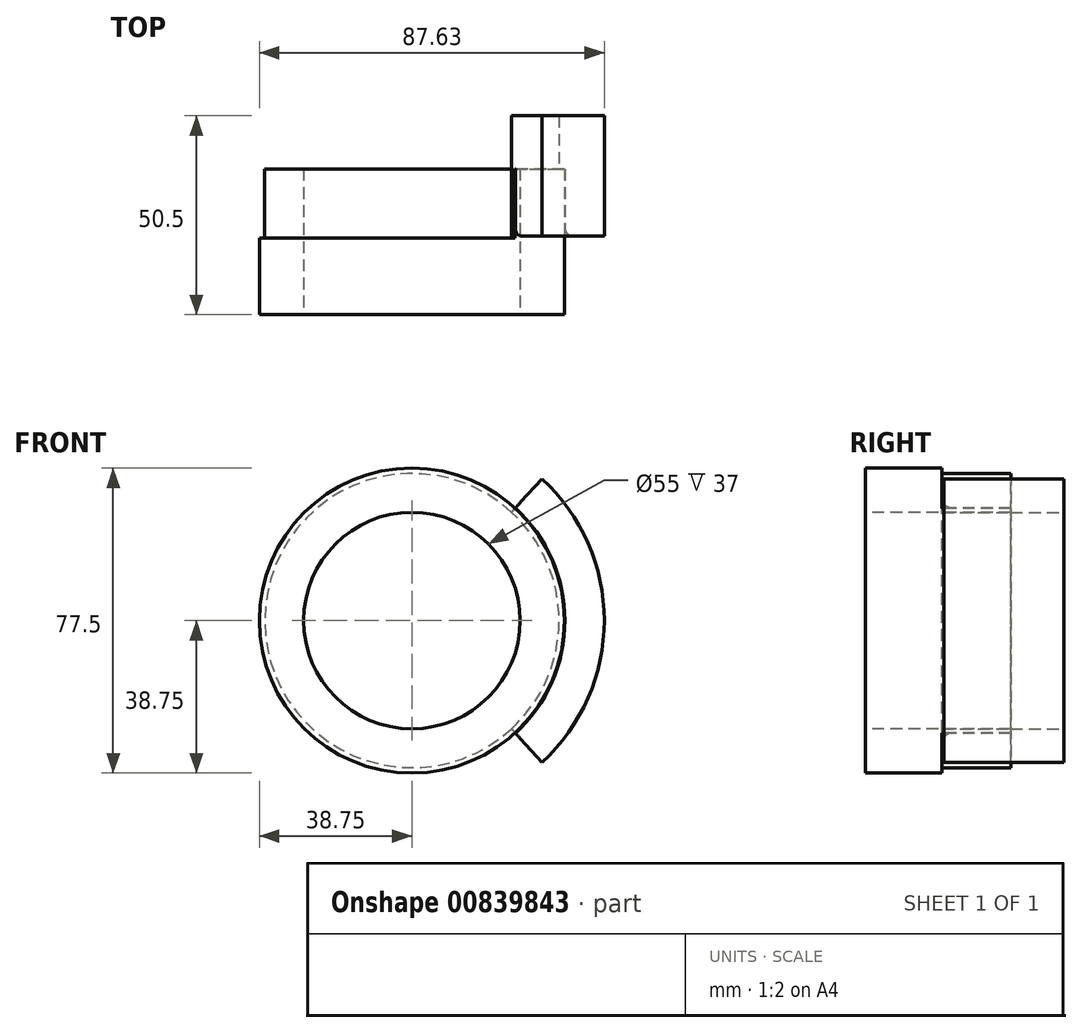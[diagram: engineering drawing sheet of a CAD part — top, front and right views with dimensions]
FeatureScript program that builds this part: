
annotation { "Feature Type Name" : "Feature", "Feature Type Description" : "" }
export const myFeature = defineFeature(function(context is Context, id is Id, definition is map)
    precondition{}
    {
        {
            var Q0;
            Q0=qCreatedBy(makeId("Front.planeOp"),FACE);
            var sketch = newSketch(context, id + "F0", { "sketchPlane" : qUnion([Q0])});
            skCircle(sketch, "E0", {"center": v(0, 0) * mm, "radius": 38.75 * mm});
            skCircle(sketch, "E1", {"center": v(0, 0) * mm, "radius": 27.5 * mm});
            skSolve(sketch);
        }
        {
            var Q0;
            Q0 = qSketchRegion(id + "F0", true);
            extrude(context, id + "F1", {"entities" : qUnion([Q0]), "oppositeDirection" : true, "depth" : 37 * mm, "offsetDistance" : 25 * mm});
        }
        {
            var Q0;
            Q0=qCreatedBy(makeId("Right.planeOp"),FACE);
            var sketch = newSketch(context, id + "F2", { "sketchPlane" : qUnion([Q0])});
            skLineSegment(sketch, "E2", {"start": v(0, 0) * mm, "end": v(0, 38.88) * mm});
            skLineSegment(sketch, "E3", {"start": v(20, 38.88) * mm, "end": v(20, 48.88) * mm});
            skLineSegment(sketch, "E4", {"start": v(20, 48.88) * mm, "end": v(50.5, 48.88) * mm});
            skLineSegment(sketch, "E5", {"start": v(50.5, 48.88) * mm, "end": v(50.5, 37.38) * mm});
            skLineSegment(sketch, "E6", {"start": v(50.5, 37.38) * mm, "end": v(37, 37.38) * mm});
            skLineSegment(sketch, "E7", {"start": v(37, 37.38) * mm, "end": v(37, 38.88) * mm});
            skLineSegment(sketch, "E8", {"start": v(37, 38.88) * mm, "end": v(20, 38.88) * mm});
            skSolve(sketch);
        }
        {
            var Q0;
            Q0=makeQuery(id+"F2.imprint","IMPRINT",FACE,{"disambiguationData":[TD([[makeQuery(id+"F2.imprint","IMPRINT",EDGE,{"derivedFrom":sQuery(id+"F2.wireOp",EDGE,"E3")}),-1.0]])]});
            var Q1;
            Q1=makeQuery(id+"F1.opExtrude","CAP_EDGE",EDGE,{"disambiguationData":[OSD([sQuery(id+"F0.wireOp",EDGE,"E0")])],"isStart":false});
            revolve(context, id + "F3", {"operationType" : NewBodyOperationType.ADD, "surfaceOperationType" : NewSurfaceOperationType.NEW, "entities" : qUnion([Q0]), "axis" : qUnion([Q1]), "revolveType" : RevolveType.FULL, "oppositeDirection" : true});
        }
        {
            var Q0;
            Q0=makeQuery(id+"F3.opRevolve","SWEPT_FACE",FACE,{"disambiguationData":[OSD([sQuery(id+"F2.wireOp",EDGE,"E5")])]});
            var sketch = newSketch(context, id + "F4", { "sketchPlane" : qUnion([Q0])});
            skLineSegment(sketch, "E9", {"start": v(-25.25, -27.5) * mm, "end": v(-33.06, -36) * mm});
            skLineSegment(sketch, "E10", {"start": v(-25.25, 27.5) * mm, "end": v(-33.06, 36) * mm});
            skPoint(sketch, "E11.center.orphan", {"position": v(0, 0) * mm});
            skArc(sketch, "E12", {"start": v(-25.28, -27.53) * mm, "mid": v(37.38, 0) * mm, "end": v(-25.28, 27.53) * mm});
            skArc(sketch, "E13", {"start": v(-33.06, -36) * mm, "mid": v(48.88, 0) * mm, "end": v(-33.06, 36) * mm});
            skSolve(sketch);
        }
        {
            var Q0;
            {var subQ0=sQuery(id+"F4.wireOp",EDGE,"E13");Q0=makeQuery(id+"F4.imprint","IMPRINT",FACE,{"disambiguationData":[TD([[makeQuery(id+"F4.imprint","IMPRINT",EDGE,{"derivedFrom":subQ0}),-1.0]])]});}
            extrude(context, id + "F5", {"entities" : qUnion([Q0]), "operationType" : NewBodyOperationType.REMOVE, "oppositeDirection" : true, "depth" : 31 * mm, "offsetDistance" : 25 * mm});
        }
        {
            var Q0;
            {var subQ0=sQuery(id+"F2.wireOp",EDGE,"E6");Q0=makeQuery(id+"F5.boolean.opBoolean","SPLIT",EDGE,{"disambiguationData":[topologyDisambiguationEdgeConnected([makeQuery(id+"F3.opRevolve","SWEPT_FACE",FACE,{"disambiguationData":[OSD([subQ0])]})])],"derivedFrom":makeQuery(id+"F3.opRevolve","SWEPT_EDGE",EDGE,{"disambiguationData":[OSD([subQ0,sQuery(id+"F2.wireOp",EDGE,"E7")])]})});}
            var Q1;
            Q1=makeQuery(id+"F3.opRevolve","SWEPT_EDGE",EDGE,{"disambiguationData":[OSD([sQuery(id+"F2.wireOp",EDGE,"E3"),sQuery(id+"F2.wireOp",EDGE,"E8")])]});
            fillet(context, id + "F6", {"entities" : qUnion([Q0, Q1]), "radius" : 2 * mm, "tangentPropagation" : true, "allowEdgeOverflow" : false});
        }
    });
